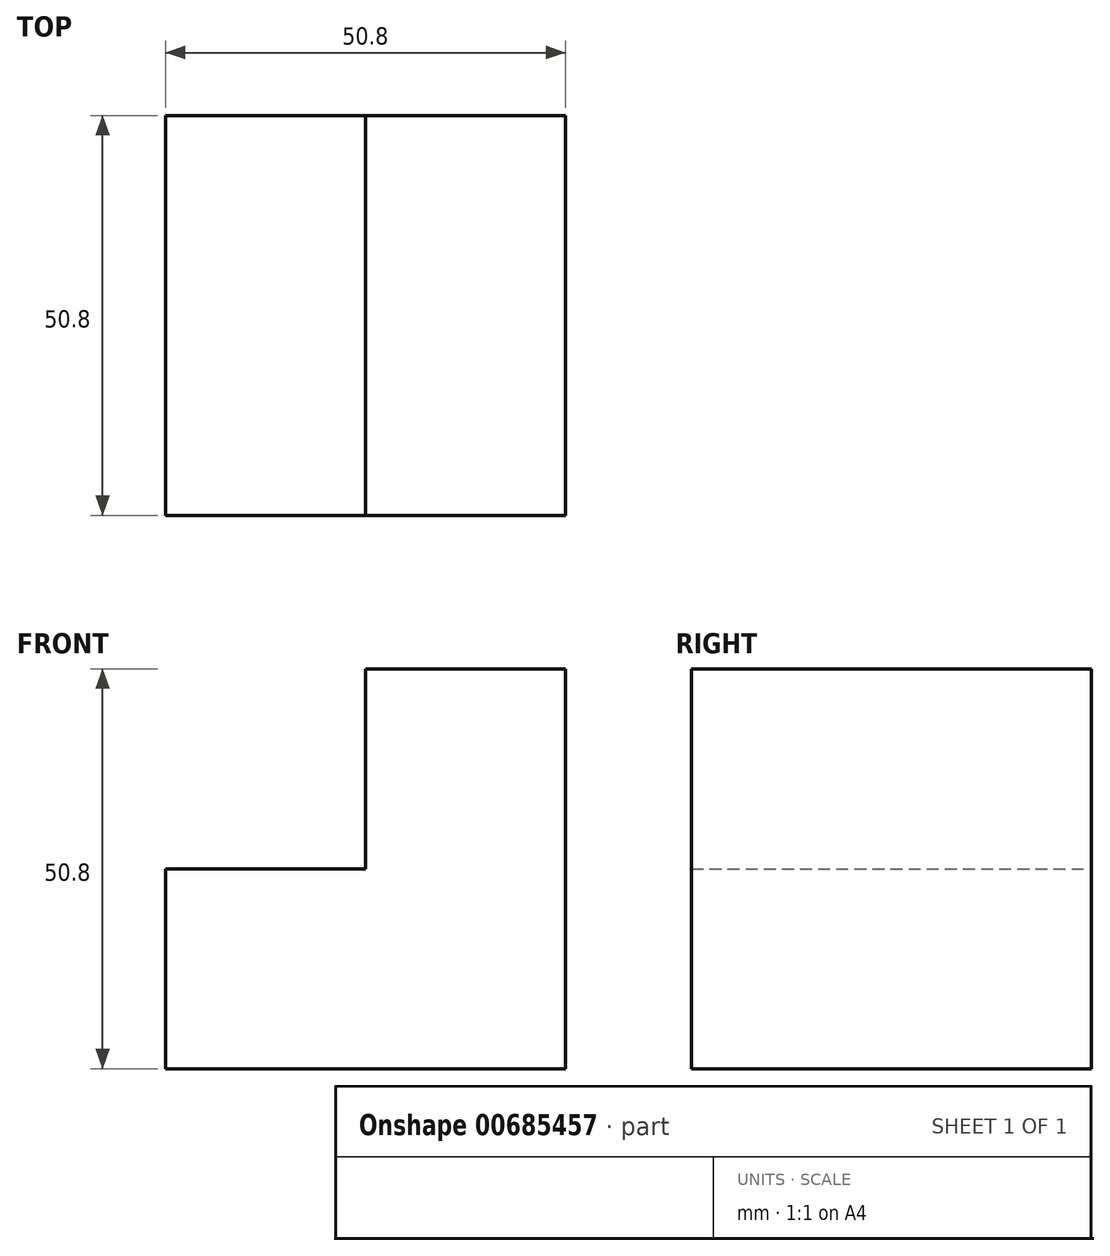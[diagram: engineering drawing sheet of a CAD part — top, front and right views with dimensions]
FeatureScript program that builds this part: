
annotation { "Feature Type Name" : "Feature", "Feature Type Description" : "" }
export const myFeature = defineFeature(function(context is Context, id is Id, definition is map)
    precondition{}
    {
        {
            var Q0;
            Q0=qCreatedBy(makeId("Front.planeOp"),FACE);
            var sketch = newSketch(context, id + "F0", { "sketchPlane" : qUnion([Q0])});
            skLineSegment(sketch, "E0", {"start": v(0, 0) * mm, "end": v(0, 50.8) * mm});
            skLineSegment(sketch, "E1", {"start": v(0, 0) * mm, "end": v(-50.8, 0) * mm});
            skLineSegment(sketch, "E2", {"start": v(-50.8, 0) * mm, "end": v(-50.8, 25.4) * mm});
            skLineSegment(sketch, "E3", {"start": v(0, 50.8) * mm, "end": v(-25.4, 50.8) * mm});
            skLineSegment(sketch, "E4", {"start": v(-50.8, 25.4) * mm, "end": v(-25.4, 25.4) * mm});
            skLineSegment(sketch, "E5", {"start": v(-25.4, 50.8) * mm, "end": v(-25.4, 25.4) * mm});
            skSolve(sketch);
        }
        {
            var Q0;
            Q0 = qSketchRegion(id + "F0", true);
            extrude(context, id + "F1", {"entities" : qUnion([Q0]), "depth" : 50.8 * mm, "offsetDistance" : 25.4 * mm});
        }
    });
